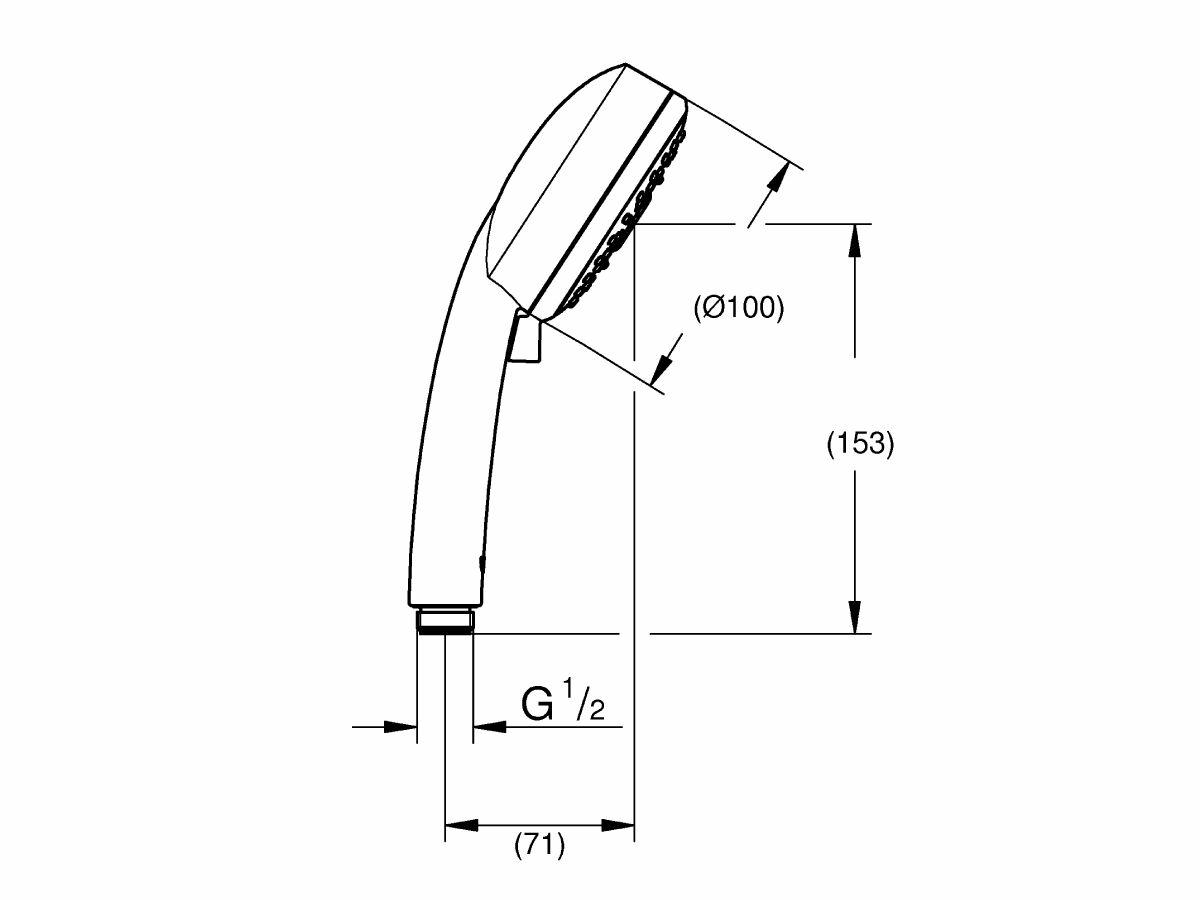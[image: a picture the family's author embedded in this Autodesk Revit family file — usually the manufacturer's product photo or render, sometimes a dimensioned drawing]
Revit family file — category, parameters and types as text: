
# Revit family: Reece_Shower_GROHE_Tempesta_Twin Shower
name_source: partatom
category: Plumbing Fixtures
revit_build: Autodesk Revit 2018 (Build: 20180329_1100(x64)
units: mm (PartAtom-declared; Revit-internal decimal feet)

## family parameters
Cut with Voids When Loaded = Yes
Host = Face
Part Type = Normal
Room Calculation Point = Yes
Round Connector Dimension = Use Diameter
Shared = Yes

## types (1)
- Chrome_White Face
    Default Elevation = 0 mm  [stored 0 ft]
    Description = GROHE Tempesta Cosmo Twin Shower White/ Chrome (3 Star)
    Disclaimer = THIS FILE IS THE PROPERTY OF THE REECE GROUP. IT MAY NOT BE REPRODUCED, REVERSE-ENGINEERED OR MODIFIED. ANY REPUBLICATION, TRANSMISSION OR DISTRIBUTION FOR THE PURPOSE OF COMMERCIALLY EXPLOITING THE FILES IS PROHIBITED.
    Keynote = Product #9508619, Reece_Shower_GROHE_Tempesta_Twin Shower - Chrome_White Face
    Manufacturer = GROHE
    Model = Tempesta
    Reece_Detail_Disclaimer = THIS FILE IS THE PROPERTY OF THE REECE GROUP. IT MAY NOT BE REPRODUCED, REVERSE-ENGINEERED OR MODIFIED. ANY REPUBLICATION, TRANSMISSION OR DISTRIBUTION FOR THE PURPOSE OF COMMERCIALLY EXPLOITING THE FILES IS PROHIBITED.
    Reece_Material_Main = Reece_Brass_Chrome
    Reece_Material_Secondary = Reece_Plastic_White
    Reece_Overall_Projection = 455 mm
    Reece_Overall_Width = 200 mm  [stored 0.656168 ft]
    Reece_Product_Brand = GROHE
    Reece_Product_Description = GROHE Tempesta Cosmo Twin Shower with Top Rail Water Inlet White/Chrome (4 Star)
    Reece_Product_Mount = Wall Mounted
    Reece_Product_Number = 9508619
    Reece_Product_Sub Brand = Tempesta
    Reece_Product_Type = Shower
    Reece_Product_Web Page = https://www.reece.com.au
    Reece_Shower_Inlet = 12 mm  [stored 0.0393701 ft]
    Type Comments = Shower
    URL = https://www.reece.com.au

note: [stored X ft] marks values corroborated as IEEE doubles in the binary element streams (Revit-internal decimal feet)

## geometry (parser evidence)
native form markers: Sweep x10
no freeform markers — native parametric forms only
